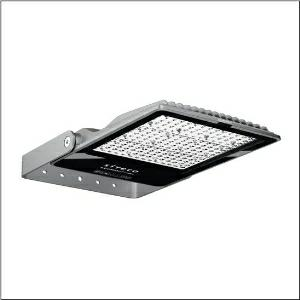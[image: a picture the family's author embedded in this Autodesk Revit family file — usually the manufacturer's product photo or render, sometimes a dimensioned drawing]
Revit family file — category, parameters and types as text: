
# Revit family: sicompact_31_midi___pl32_5xa7581d2k23_8b39
name_source: partatom
category: Lighting Fixtures
units: mm (PartAtom-declared; Revit-internal decimal feet)

## family parameters
Cut with Voids When Loaded = No
Host = Face
Light Source = No
Part Type = Normal
Room Calculation Point = No
Round Connector Dimension = Use Diameter
Shared = No

## types (1)
- SiCompact 31 midi  PL32 (1 x LED, 27000 lm, 165 W, 4000K)
    Apparent Load = 165 VA
    CIE Flux Codes = 32 69 98 100 100
    Color Rendering = 70
    Color Temperature = 4000K
    Default Elevation = 1800 mm
    Description = SiCompact 31 midi, floodlight, primary light control with lens, of plastic, of toughened safety glass, transparent, light distribution: PL32, light emission: direct distribution, primary light characteristic: asymmetric, installation type: surface-mounted, LED, High Power LED, rated luminous flux: 27.000lm, luminous efficacy: 164lm/W, light colour: 740, colour temperature: 4000K, control gear: ON/OFF, with cable, 3x 1.5mm², mains connection: 220..240V, AC, 50/60Hz, connection cable pre-assembled, cable length: 2m, rated input power: 165W, of diecast aluminium, specular, metallic grey (RAL 9006), length: 560mm, width: 330mm, height: 62mm, bracket, of sheet steel, coated, metallic grey (RAL 9006), ON/OFF, protection rating (complete): IP66, insulation class (complete): insulation class I (protective earthing), certification: CE, ENEC, impact resistance: IK08, permissible operating ambient temperature: -40..+45°C, packaging unit: 1 piece

Light Distribution: PL32
    Height = 62 mm  [stored 0.203412 ft]
    Lamp = 1 x LED
    Lamp Light Flux = 27000 lm
    Lamp Power = 165 W
    Lamp count = 1
    Length = 560 mm
    Luminous efficacy = 164 lm/W
    Manufacturer = Siteco
    ModVariant = No
    Model = 5XA7581D2K23
    Mounting Place = Wall
    Mounting Type = Surface mounted
    Number of Poles = 1
    OnlyDefault = Yes
    Power Factor = 1
    Product Name = SiCompact 31 midi | PL32
    Product group = floodlight | wall mounted
    ProductGroupID = 2002
    Protection Class = Protection class I
    Protection Degree = IP 66
    RLX_Detail_Level = 1
    RLX_Emergency_Light_Flux = 0 lm
    RLX_Emergency_Type = 0
    RLX_Emergency_Type_DB = No
    RlxData = <blob elided: 98269 chars, md5=5cf4306a>
    Socket = socket
    Standby Power = 0 W
    System Light Flux = 27000 lm
    System Power = 165 W
    Type Comments = Product without accessories
    Type Image = l_1006415.jpg
    URL = http://relux.com
    VarID = ---
    Voltage = 0 V
    Weight = 0.00 kg
    Width = 333 mm

note: [stored X ft] marks values corroborated as IEEE doubles in the binary element streams (Revit-internal decimal feet)

## geometry (parser evidence)
native form markers: Blend x4, Sweep x11
no freeform markers — native parametric forms only
